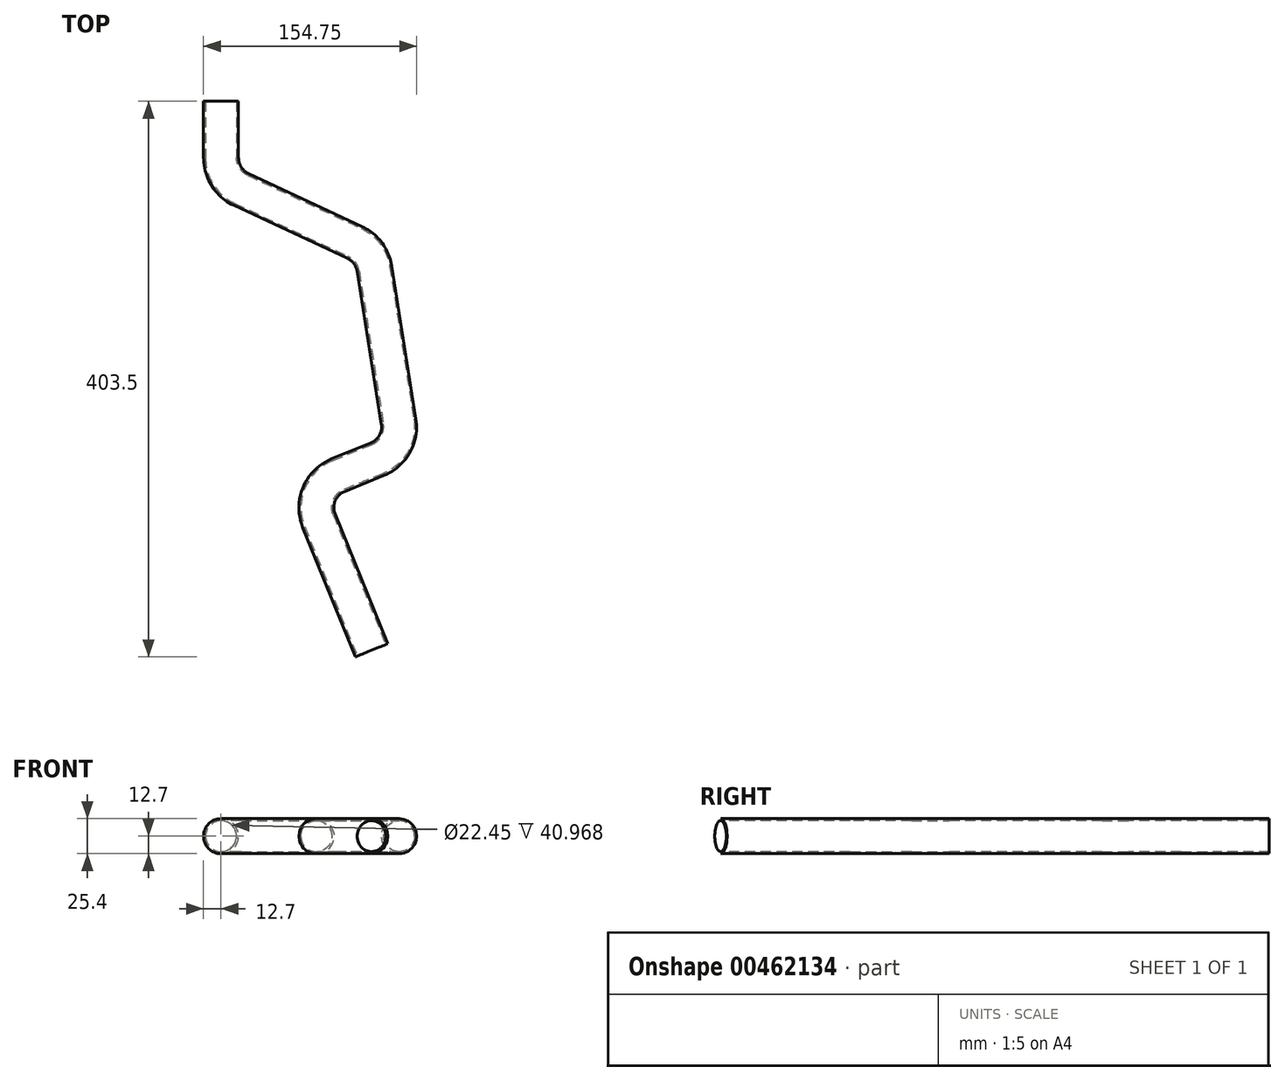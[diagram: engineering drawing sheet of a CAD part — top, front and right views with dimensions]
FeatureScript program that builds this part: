
annotation { "Feature Type Name" : "Feature", "Feature Type Description" : "" }
export const myFeature = defineFeature(function(context is Context, id is Id, definition is map)
    precondition{}
    {
        {
            var Q0;
            Q0=qCreatedBy(makeId("Top.planeOp"),FACE);
            var sketch = newSketch(context, id + "F0", { "sketchPlane" : qUnion([Q0])});
            skLineSegment(sketch, "E0", {"start": v(0, 0) * mm, "end": v(0, -60.02) * mm});
            skLineSegment(sketch, "E1", {"start": v(14.67, -83.04) * mm, "end": v(97.1, -121.48) * mm});
            skLineSegment(sketch, "E2", {"start": v(111.46, -140.53) * mm, "end": v(129.04, -251.52) * mm});
            skLineSegment(sketch, "E3", {"start": v(113.5, -279.03) * mm, "end": v(85.12, -290.54) * mm});
            skLineSegment(sketch, "E4", {"start": v(71.14, -323.63) * mm, "end": v(109.35, -417.77) * mm});
            skPoint(sketch, "E5.visualSharp", {"position": v(61.59, -300.1) * mm});
            skArc(sketch, "E5.filletArc", {"start": v(85.12, -290.54) * mm, "mid": v(71.28, -304.2) * mm, "end": v(71.14, -323.63) * mm});
            skPoint(sketch, "E6.visualSharp", {"position": v(132.2, -271.44) * mm});
            skArc(sketch, "E6.filletArc", {"start": v(113.5, -279.03) * mm, "mid": v(126.07, -267.98) * mm, "end": v(129.04, -251.52) * mm});
            skPoint(sketch, "E7.visualSharp", {"position": v(109.35, -127.19) * mm});
            skArc(sketch, "E7.filletArc", {"start": v(111.46, -140.53) * mm, "mid": v(106.66, -129.22) * mm, "end": v(97.1, -121.48) * mm});
            skPoint(sketch, "E8.visualSharp", {"position": v(0, -76.2) * mm});
            skArc(sketch, "E8.filletArc", {"start": v(0, -60.02) * mm, "mid": v(3.98, -73.67) * mm, "end": v(14.67, -83.04) * mm});
            skSolve(sketch);
        }
        {
            var Q0;
            Q0=qCreatedBy(makeId("Front.planeOp"),FACE);
            var sketch = newSketch(context, id + "F1", { "sketchPlane" : qUnion([Q0])});
            skCircle(sketch, "E9", {"center": v(0, 0) * mm, "radius": 12.7 * mm});
            skSolve(sketch);
        }
        {
            var Q0;
            Q0 = qSketchRegion(id + "F1", true);
            var Q1;
            Q1 = qConstructionFilter(qBodyType(qCreatedBy(id + "F0" ,EDGE), BodyType.WIRE), ConstructionObject.NO);
            sweep(context, id + "F2", {"profiles" : qUnion([Q0]), "path" : qUnion([Q1])});
        }
        {
            var Q0;
            Q0=makeQuery(id+"F2.opSweep","CAP_FACE",FACE,{"disambiguationData":[OSD([sQuery(id+"F0.wireOp",VERTEX,"E0.start"),sQuery(id+"F1.wireOp",EDGE,"E9")])],"isStart":true});
            var Q1;
            Q1=makeQuery(id+"F2.opSweep","CAP_FACE",FACE,{"disambiguationData":[OSD([sQuery(id+"F0.wireOp",VERTEX,"E4.end"),sQuery(id+"F1.wireOp",EDGE,"E9")])],"isStart":false});
            shell(context, id + "F3", {"entities" : qUnion([Q0, Q1]), "thickness" : 1.47 * mm});
        }
        {
            var Q0;
            Q0=makeQuery(id+"F2.opSweep","CAP_FACE",FACE,{"disambiguationData":[OSD([sQuery(id+"F0.wireOp",VERTEX,"E0.start"),sQuery(id+"F1.wireOp",EDGE,"E9")])],"isStart":true});
            var sketch = newSketch(context, id + "F4", { "sketchPlane" : qUnion([Q0])});
            skCircle(sketch, "E10", {"center": v(0, 0) * mm, "radius": 19.05 * mm});
            skSolve(sketch);
        }
        {
            var Q0;
            Q0 = qSketchRegion(id + "F4", true);
            extrude(context, id + "F5", {"entities" : qUnion([Q0]), "operationType" : NewBodyOperationType.REMOVE, "oppositeDirection" : true, "depth" : 19.05 * mm});
        }
    });
